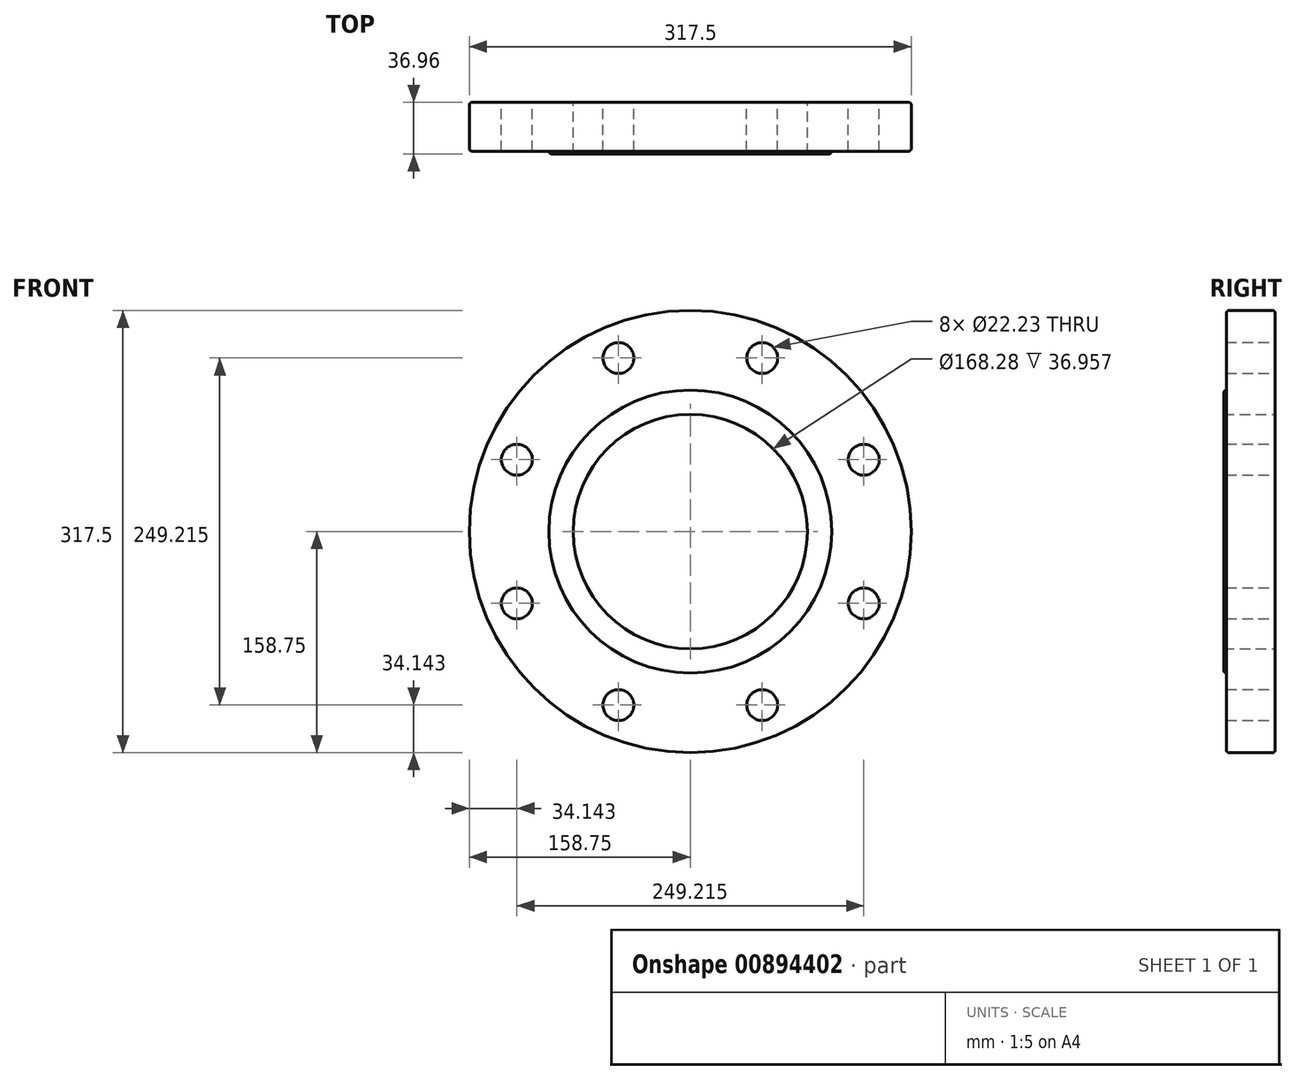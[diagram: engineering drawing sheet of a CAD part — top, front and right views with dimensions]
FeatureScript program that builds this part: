
annotation { "Feature Type Name" : "Feature", "Feature Type Description" : "" }
export const myFeature = defineFeature(function(context is Context, id is Id, definition is map)
    precondition{}
    {
        {
            var Q0;
            Q0=qCreatedBy(makeId("Front.planeOp"),FACE);
            var sketch = newSketch(context, id + "F0", { "sketchPlane" : qUnion([Q0])});
            skCircle(sketch, "E0", {"center": v(0, 0) * mm, "radius": 158.75 * mm});
            skCircle(sketch, "E1", {"center": v(0, 0) * mm, "radius": 84.14 * mm});
            skCircle(sketch, "E2", {"center": v(0, 0) * mm, "radius": 134.87 * mm, "construction": true});
            skLineSegment(sketch, "E3", {"start": v(0, 0) * mm, "end": v(0, 164.86) * mm, "construction": true});
            skLineSegment(sketch, "E4", {"start": v(0, 0) * mm, "end": v(65.86, 159) * mm, "construction": true});
            skCircle(sketch, "E5", {"center": v(51.61, 124.6) * mm, "radius": 11.11 * mm});
            skCircle(sketch, "E6.1.0", {"center": v(-51.61, 124.6) * mm, "radius": 11.11 * mm});
            skCircle(sketch, "E6.2.0", {"center": v(-124.6, 51.61) * mm, "radius": 11.11 * mm});
            skCircle(sketch, "E6.3.0", {"center": v(-124.6, -51.61) * mm, "radius": 11.11 * mm});
            skCircle(sketch, "E6.4.0", {"center": v(-51.61, -124.6) * mm, "radius": 11.11 * mm});
            skCircle(sketch, "E6.5.0", {"center": v(51.61, -124.6) * mm, "radius": 11.11 * mm});
            skCircle(sketch, "E6.6.0", {"center": v(124.6, -51.61) * mm, "radius": 11.11 * mm});
            skCircle(sketch, "E6.7.0", {"center": v(124.6, 51.61) * mm, "radius": 11.11 * mm});
            skSolve(sketch);
        }
        {
            var Q0;
            Q0 = qSketchRegion(id + "F0", true);
            extrude(context, id + "F1", {"entities" : qUnion([Q0]), "depth" : 35.05 * mm, "offsetDistance" : 25.4 * mm});
        }
        {
            var Q0;
            Q0=makeQuery(id+"F1.opExtrude","CAP_FACE",FACE,{"disambiguationData":[OSD([sQuery(id+"F0.wireOp",EDGE,"E0"),sQuery(id+"F0.wireOp",EDGE,"E1"),sQuery(id+"F0.wireOp",EDGE,"E5"),sQuery(id+"F0.wireOp",EDGE,"E6.1.0"),sQuery(id+"F0.wireOp",EDGE,"E6.2.0"),sQuery(id+"F0.wireOp",EDGE,"E6.3.0"),sQuery(id+"F0.wireOp",EDGE,"E6.4.0"),sQuery(id+"F0.wireOp",EDGE,"E6.5.0"),sQuery(id+"F0.wireOp",EDGE,"E6.6.0"),sQuery(id+"F0.wireOp",EDGE,"E6.7.0")])],"isStart":false});
            var sketch = newSketch(context, id + "F2", { "sketchPlane" : qUnion([Q0])});
            skCircle(sketch, "E7", {"center": v(0, 0) * mm, "radius": 84.14 * mm});
            skCircle(sketch, "E8", {"center": v(0, 0) * mm, "radius": 101.6 * mm});
            skSolve(sketch);
        }
        {
            var Q0;
            Q0 = qSketchRegion(id + "F2", true);
            extrude(context, id + "F3", {"entities" : qUnion([Q0]), "operationType" : NewBodyOperationType.ADD, "depth" : 1.9 * mm, "offsetDistance" : 25.4 * mm});
        }
        {
            var Q0;
            Q0=makeQuery(id+"F1.opExtrude","CAP_EDGE",EDGE,{"disambiguationData":[OSD([sQuery(id+"F0.wireOp",EDGE,"E0")])],"isStart":false});
            var Q1;
            Q1=makeQuery(id+"F1.opExtrude","CAP_EDGE",EDGE,{"disambiguationData":[OSD([sQuery(id+"F0.wireOp",EDGE,"E0")])],"isStart":true});
            var Q2;
            Q2=makeQuery(id+"F3.opExtrude","CAP_EDGE",EDGE,{"disambiguationData":[OSD([sQuery(id+"F2.wireOp",EDGE,"E8")])],"isStart":false});
            fillet(context, id + "F4", {"entities" : qUnion([Q0, Q1, Q2]), "radius" : 1.9 * mm, "tangentPropagation" : true, "allowEdgeOverflow" : false});
        }
    });
